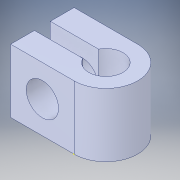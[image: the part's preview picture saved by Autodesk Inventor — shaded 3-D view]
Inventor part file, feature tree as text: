
AUTODESK INVENTOR PART (.ipt)
format: ipt  version: 2018 (Build 220112000, 112)  size: 126,976 bytes
history: native  units: in
note: dims shown in document units (in); Inventor stores cm internally (conversion verified against a paired STEP export)
features: sketch x3, extrude x2, other x1
ambient origin geometry x8: Origin, YZ Plane, XZ Plane, XY Plane, X Axis, Y Axis, Z Axis, Center Point
bodies: Solid1 (feature_tree)
feature tree (6):
  extrude  "Extrusion1"  TaperAngle=0.0deg  [1 undecoded]
  sketch  "Sketch2"  dims[d5=0.2539in d6=0.0in d7=0.0in]
  extrude  "Extrusion2"  TaperAngle=0.0deg  [1 undecoded]
  sketch  "Sketch1"  dims[d1=0.2697in d2=0.0in d3=0.0in]
  sketch  "Sketch3"
  other  "Cut-Extrude1"
note: 2 required parameter values undecoded (feature->parameter linkage not recoverable at this tier; creation-order binding heuristic only, values carry confidence <= 0.55)
